# Revit family: HVAC-Chilled_Beam-Dadanco-ACB10
name_source: partatom
category: Mechanical Equipment
units: mm (PartAtom-declared; Revit-internal decimal feet)

## family parameters
Always vertical = Yes
Cut with Voids When Loaded = No
Maintain Annotation Orientation = No
OmniClass Number = 23.75.70.17.31
OmniClass Title = Induction Units
Part Type = Normal
Room Calculation Point = No
Round Connector Dimension = Use Radius
Shared = No
Work Plane-Based = No

## types (7) — shared parameters
2 Pipe Coil Configuration = Yes
2 or 4 pipe = 2
4 Pipe Coil Configuration = No
Assembly Code = D3040100
CWF = 0.0 GPM
CWPD = 0.00 ftH2O
Cooling Primary Air Dry Bulb = 0 °F
Cooling Primary Air Wet Bulb = 0 °F
Cooling Room Dry Bulb = 0 °F
Cooling Supply Air Temperature = 0 °F
Default Elevation = 0"
Description = Active Chilled Beam
Documentation Link = https://www.dadanco.com
HWF = 0.0 GPM
HWPD = 0.00 ftH2O
Heating Primary Air Dry Bulb = 0 °F
Heating Primary Air Wet Bulb = 0 °F
Heating Room Dry Bulb = 0 °F
Heating Supply Air Temperature = 0 °F
Housing Material = Metal-Dadanco-Steel-Galvanized
Latent Cooling = 0.0 Btu/h
Manufacturer = Dadanco
Model = ACB10
Net Unit Cooling Sensible = 0.0 Btu/h
Net Unit Heating Sensible = 0.0 Btu/h
PA = 0 CFM
PASP = 0.00 in-wg
Primary Air Inlet Size = 4"
Primary Air Radius = 2"
Revision Date = 1/29/2025
SCHW Temp Out = 0 °F
SCHW Temperature = 0 °F
SHHW Temp Out = 0 °F
SHHW Temperature = 0 °F
Secondary Air Sensible Cooling = 0.0 Btu/h
Secondary Air Sensible Heating = 0.0 Btu/h
Supply Air = 0 CFM
Total Cooling Capacity = 0.0 Btu/h
Tube Material = Metal-Dadanco-Copper-Satin
URL = http://www.dadanco.com
Unit Height = 6 11/32"
Unit Width = 17 13/16"
zero-valued in all types: Cooling Room Relative Humidity

## per-type parameters (varying)
| type | Keynote | Nominal Unit Length | Overall Unit Length | Type Comments | Unit Length | Unit Weight |
| 4' Nominal Length |  | 48" | 44" |  | 40" | 42 lb |
| 3' Nominal Length | 23 37 00.A1 | 36" | 36" | Horizonatally Mounted Induction Unit | 32" | 35 lb |
| 5' Nominal Length | 23 37 00.A1 | 60" | 56" | Horizonatally Mounted Induction Unit | 52" | 49 lb |
| 6' Nominal Length | 23 37 00.A1 | 72" | 68" | Horizonatally Mounted Induction Unit | 64" | 56 lb |
| 2' Nominal Length | 23 37 00.A1 | 24" | 28" | Horizonatally Mounted Induction Unit | 24" | 27 lb |
| 7' Nominal Length | 23 37 00.A1 | 84" | 80" | Horizonatally Mounted Induction Unit | 76" | 63 lb |
| 8' Nominal Length | 23 37 00.A1 | 96" | 92" | Horizonatally Mounted Induction Unit | 88" | 70 lb |

## geometry (parser evidence)
native form markers: Sweep x3
no freeform markers — native parametric forms only
